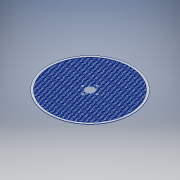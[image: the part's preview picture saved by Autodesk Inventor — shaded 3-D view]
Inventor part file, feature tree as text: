
AUTODESK INVENTOR PART (.ipt)
format: ipt  version: 2018 (Build 220112000, 112)  size: 3,430,912 bytes
history: native  units: mm
features: extrude x5, sketch x4, pattern_linear x2
ambient origin geometry x8: Origin, YZ Plane, XZ Plane, XY Plane, X Axis, Y Axis, Z Axis, Center Point
bodies: Solid1 (feature_tree)
feature tree (11):
  sketch  "Sketch1"  dims[d0=508.0mm d1=482.6mm]
  extrude  "Extrusion1"  Depth=482.6mm
  pattern_linear  "Rectangular Pattern1"  Count1=10 Spacing1=10.5mm
  extrude  "Extrusion4"  Depth=105.0mm
  pattern_linear  "Rectangular Pattern2"  Spacing1=10.0mm  [1 undecoded]
  extrude  "Extrusion2"  Depth=2.0mm TaperAngle=0.0deg
  extrude  "Extrusion3"  TaperAngle=30.0deg  [1 undecoded]
  extrude  "Extrusion5"  Depth=10.5mm
  sketch  "Sketch2"  dims[d2=508.0mm]
  sketch  "Sketch3"  dims[d3=3.0mm d4=100.0mm d6=10.5mm d7=10.0mm d9=10.0mm]
  sketch  "Sketch4"  dims[d11=0.75mm d12=0.0mm d13=50.0mm d15=105.0mm d19=10.0mm d20=0.0mm d21=2.0mm d22=0.0mm d23=30.0deg d24=100.0mm d26=10.5mm d27=10.0mm d29=10.0mm d31=0.75mm d32=0.0mm d33=50.0mm d35=105.0mm d37=40.0mm d38=55.0mm d39=360.0deg d40=87.3125mm d41=15.875mm d42=0.0mm d43=0.0mm]
note: 2 required parameter values undecoded (feature->parameter linkage not recoverable at this tier; creation-order binding heuristic only, values carry confidence <= 0.55)
